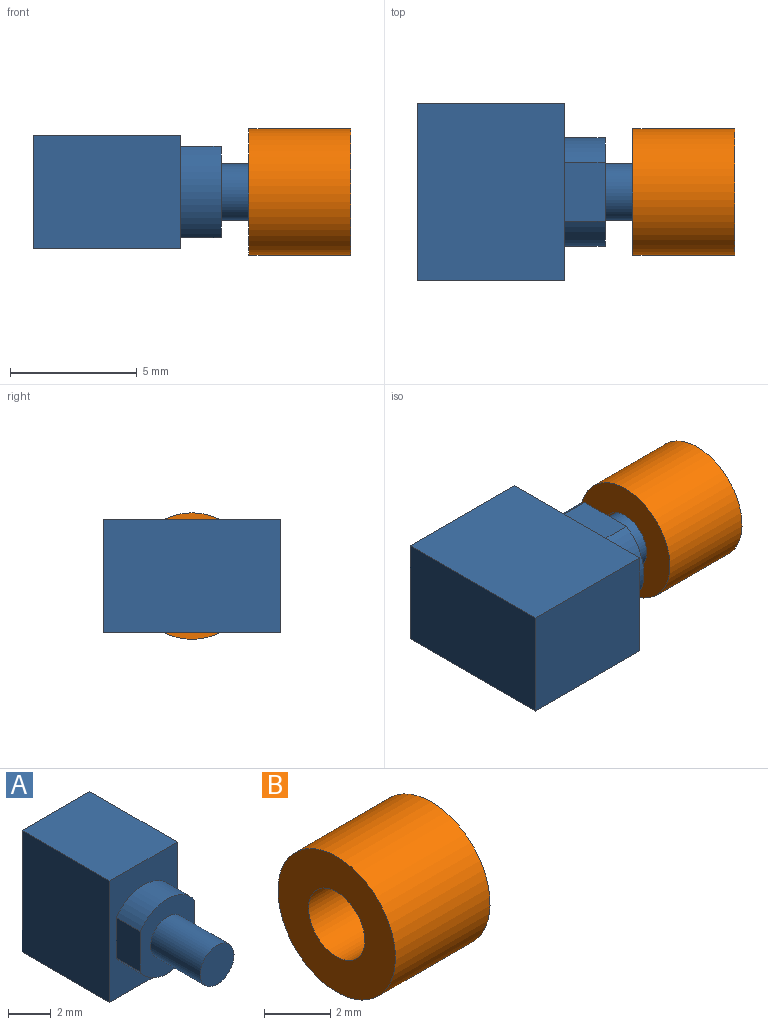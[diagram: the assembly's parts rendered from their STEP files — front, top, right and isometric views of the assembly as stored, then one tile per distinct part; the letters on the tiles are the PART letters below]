
ASSEMBLY  parts=2 mates=1
PART A: 13 faces, bbox 4.5x10.7x7 mm
  f0: plane 7x4.5mm, normal (0,-1,0), area 18.1mm2, adj f1,f2,f3,f4,f6,f7,f8,f9
  f1: plane 5.83x4.5mm, normal (0,0,1), area 26.2mm2, adj f0,f2,f4,f5
  f2: plane 7x5.83mm, normal (-1,0,0), area 40.8mm2, adj f0,f1,f3,f5
  f3: plane 5.83x4.5mm, normal (0,0,-1), area 26.2mm2, adj f0,f2,f4,f5
  f4: plane 7x5.83mm, normal (1,0,0), area 40.8mm2, adj f0,f1,f3,f5
  f5: plane 7x4.5mm, normal (0,1,0), area 31.5mm2, adj f1,f2,f3,f4
  f6: plane 2.33x1.6mm, normal (1,0,0), area 3.7mm2, adj f0,f7,f9,f10
  f7: cylinder r=2.15mm len=3.61mm, axis (0,1,0), area 6.9mm2, adj f0,f6,f8,f10
  f8: plane 2.33x1.6mm, normal (-1,0,0), area 3.7mm2, adj f0,f7,f9,f10
  f9: cylinder r=2.15mm len=3.61mm, axis (0,1,0), area 6.9mm2, adj f0,f6,f8,f10
  f10: plane 4.3x3.61mm, normal (0,-1,0), area 9.5mm2, adj f6,f7,f8,f9,f11
  f11: cylinder r=1.12mm len=3.3mm, axis (0,1,0), area 23.3mm2, adj f10,f12
  f12: plane 2.25x2.25mm, normal (0,-1,0), area 4mm2, adj f11
PART B: 5 faces, bbox 4x5x5 mm
  f0: plane 5x5mm, normal (1,0,0), area 19.6mm2, adj f1
  f1: cylinder r=2.5mm len=5mm, axis (-1,0,0), area 63.3mm2, adj f0,f2
  f2: plane 5x5mm, normal (-1,0,0), area 15.1mm2, adj f1,f3
  f3: cylinder r=1.2mm len=2.4mm, axis (-1,0,0), area 16.6mm2, adj f2,f4
  f4: plane 2.4x2.4mm, normal (-1,0,0), area 4.5mm2, adj f3
PLACE A rot(axis=(0.58,-0.58,0.58),120deg) t=(-16.2,-7.95,10.37)mm
PLACE B t=(-11.6,-4.45,1.03)mm
MATE fastened A.f7 <-> B.f1  axis (-1,0,0) through (-5.47,-4.45,1.03)mm
